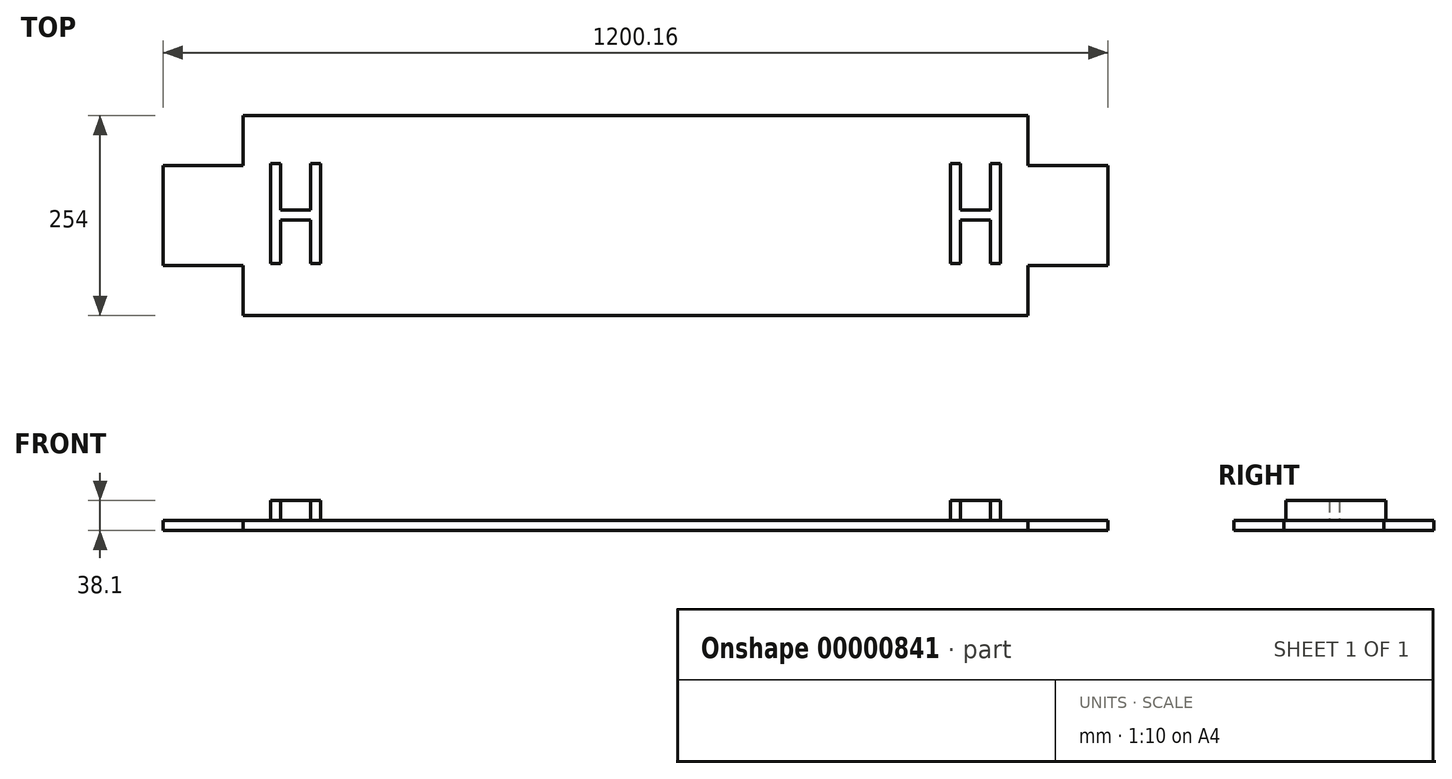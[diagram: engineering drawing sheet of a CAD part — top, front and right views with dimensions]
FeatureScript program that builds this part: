
annotation { "Feature Type Name" : "Feature", "Feature Type Description" : "" }
export const myFeature = defineFeature(function(context is Context, id is Id, definition is map)
    precondition{}
    {
        {
            var Q0;
            Q0=qCreatedBy(makeId("Top.planeOp"),FACE);
            var sketch = newSketch(context, id + "F0", { "sketchPlane" : qUnion([Q0])});
            skLineSegment(sketch, "E0.bottom", {"start": v(0, 0) * mm, "end": v(-498.48, 0) * mm});
            skLineSegment(sketch, "E0.top", {"start": v(0, 254) * mm, "end": v(-498.48, 254) * mm});
            skLineSegment(sketch, "E0.left", {"start": v(0, 0) * mm, "end": v(0, 254) * mm});
            skLineSegment(sketch, "E1.bottom", {"start": v(-498.48, 190.5) * mm, "end": v(-600.08, 190.5) * mm});
            skLineSegment(sketch, "E1.top", {"start": v(-498.48, 63.5) * mm, "end": v(-600.08, 63.5) * mm});
            skLineSegment(sketch, "E1.right", {"start": v(-600.08, 190.5) * mm, "end": v(-600.08, 63.5) * mm});
            skLineSegment(sketch, "E2.trimOffspring", {"start": v(-498.48, 190.5) * mm, "end": v(-498.48, 254) * mm});
            skLineSegment(sketch, "E3", {"start": v(-498.48, 0) * mm, "end": v(-498.48, 63.5) * mm});
            skLineSegment(sketch, "E4", {"start": v(-600.08, 127) * mm, "end": v(0, 127) * mm, "construction": true});
            skLineSegment(sketch, "E5.bottom", {"start": v(-463.55, 192.97) * mm, "end": v(-450.85, 192.97) * mm});
            skLineSegment(sketch, "E5.top", {"start": v(-463.55, 65.97) * mm, "end": v(-450.85, 65.97) * mm, "construction": true});
            skLineSegment(sketch, "E5.left", {"start": v(-463.55, 192.97) * mm, "end": v(-463.55, 65.97) * mm, "construction": true});
            skLineSegment(sketch, "E5.right", {"start": v(-450.85, 192.97) * mm, "end": v(-450.85, 65.97) * mm, "construction": true});
            skLineSegment(sketch, "E6.bottom", {"start": v(-412.75, 192.97) * mm, "end": v(-400.05, 192.97) * mm, "construction": true});
            skLineSegment(sketch, "E6.top", {"start": v(-412.75, 65.97) * mm, "end": v(-400.05, 65.97) * mm, "construction": true});
            skLineSegment(sketch, "E6.left", {"start": v(-412.75, 192.97) * mm, "end": v(-412.75, 65.97) * mm, "construction": true});
            skLineSegment(sketch, "E6.right", {"start": v(-400.05, 192.97) * mm, "end": v(-400.05, 65.97) * mm, "construction": true});
            skLineSegment(sketch, "E7.bottom", {"start": v(-450.85, 133.94) * mm, "end": v(-412.75, 133.94) * mm, "construction": true});
            skLineSegment(sketch, "E7.top", {"start": v(-450.85, 121.24) * mm, "end": v(-412.75, 121.24) * mm, "construction": true});
            skLineSegment(sketch, "E7.left", {"start": v(-450.85, 133.94) * mm, "end": v(-450.85, 121.24) * mm, "construction": true});
            skLineSegment(sketch, "E7.right", {"start": v(-412.75, 133.94) * mm, "end": v(-412.75, 121.24) * mm, "construction": true});
            skSolve(sketch);
        }
        {
            var Q0;
            Q0=makeQuery(id+"F0.imprint","IMPRINT",FACE,{"disambiguationData":[TD([[makeQuery(id+"F0.imprint","IMPRINT",EDGE,{"derivedFrom":sQuery(id+"F0.wireOp",EDGE,"E0.bottom")}),-1.0]])]});
            var sketch = newSketch(context, id + "F1", { "sketchPlane" : qUnion([Q0])});
            skLineSegment(sketch, "E8", {"start": v(-463.55, 192.97) * mm, "end": v(-450.85, 192.97) * mm});
            skLineSegment(sketch, "E9", {"start": v(-450.85, 192.97) * mm, "end": v(-450.85, 133.94) * mm});
            skLineSegment(sketch, "E10", {"start": v(-450.85, 133.94) * mm, "end": v(-412.75, 133.94) * mm});
            skLineSegment(sketch, "E11", {"start": v(-412.75, 133.94) * mm, "end": v(-412.75, 192.97) * mm});
            skLineSegment(sketch, "E12", {"start": v(-412.75, 192.97) * mm, "end": v(-400.05, 192.97) * mm});
            skLineSegment(sketch, "E13", {"start": v(-400.05, 192.97) * mm, "end": v(-400.05, 65.97) * mm});
            skLineSegment(sketch, "E14", {"start": v(-400.05, 65.97) * mm, "end": v(-412.75, 65.97) * mm});
            skLineSegment(sketch, "E15", {"start": v(-412.75, 65.97) * mm, "end": v(-412.75, 121.24) * mm});
            skLineSegment(sketch, "E16", {"start": v(-412.75, 121.24) * mm, "end": v(-450.85, 121.24) * mm});
            skLineSegment(sketch, "E17", {"start": v(-450.85, 121.24) * mm, "end": v(-450.85, 65.97) * mm});
            skLineSegment(sketch, "E18", {"start": v(-450.85, 65.97) * mm, "end": v(-463.55, 65.97) * mm});
            skLineSegment(sketch, "E19", {"start": v(-463.55, 65.97) * mm, "end": v(-463.55, 192.97) * mm});
            skSolve(sketch);
        }
        {
            var Q0;
            {var subQ3=sQuery(id+"F0.wireOp",EDGE,"E0.bottom");Q0=makeQuery(id+"F0.imprint","IMPRINT",FACE,{"disambiguationData":[TD([[makeQuery(id+"F0.imprint","IMPRINT",EDGE,{"derivedFrom":subQ3}),-1.0]])]});}
            extrude(context, id + "F2", {"entities" : qUnion([Q0]), "oppositeDirection" : true, "depth" : 12.7 * mm});
        }
        {
            var Q0;
            Q0 = qSketchRegion(id + "F1", true);
            extrude(context, id + "F3", {"entities" : qUnion([Q0]), "operationType" : NewBodyOperationType.ADD, "depth" : 25.4 * mm});
        }
        {
            var Q0;
            Q0=makeQuery(id+"F2.opExtrude","SWEPT_BODY",BODY,{"disambiguationData":[OSD([sQuery(id+"F0.wireOp",EDGE,"E0.bottom"),sQuery(id+"F0.wireOp",EDGE,"E0.top"),sQuery(id+"F0.wireOp",EDGE,"E0.left"),sQuery(id+"F0.wireOp",EDGE,"E1.bottom"),sQuery(id+"F0.wireOp",EDGE,"E1.top"),sQuery(id+"F0.wireOp",EDGE,"E1.right"),sQuery(id+"F0.wireOp",EDGE,"E2.trimOffspring"),sQuery(id+"F0.wireOp",EDGE,"E3")])]});
            var Q1;
            Q1=makeQuery(id+"F2.opExtrude","SWEPT_FACE",FACE,{"disambiguationData":[OSD([sQuery(id+"F0.wireOp",EDGE,"E0.left")])]});
            mirror(context, id + "F4", {"operationType" : NewBodyOperationType.ADD, "entities" : qUnion([Q0]), "mirrorPlane" : qUnion([Q1])});
        }
    });
